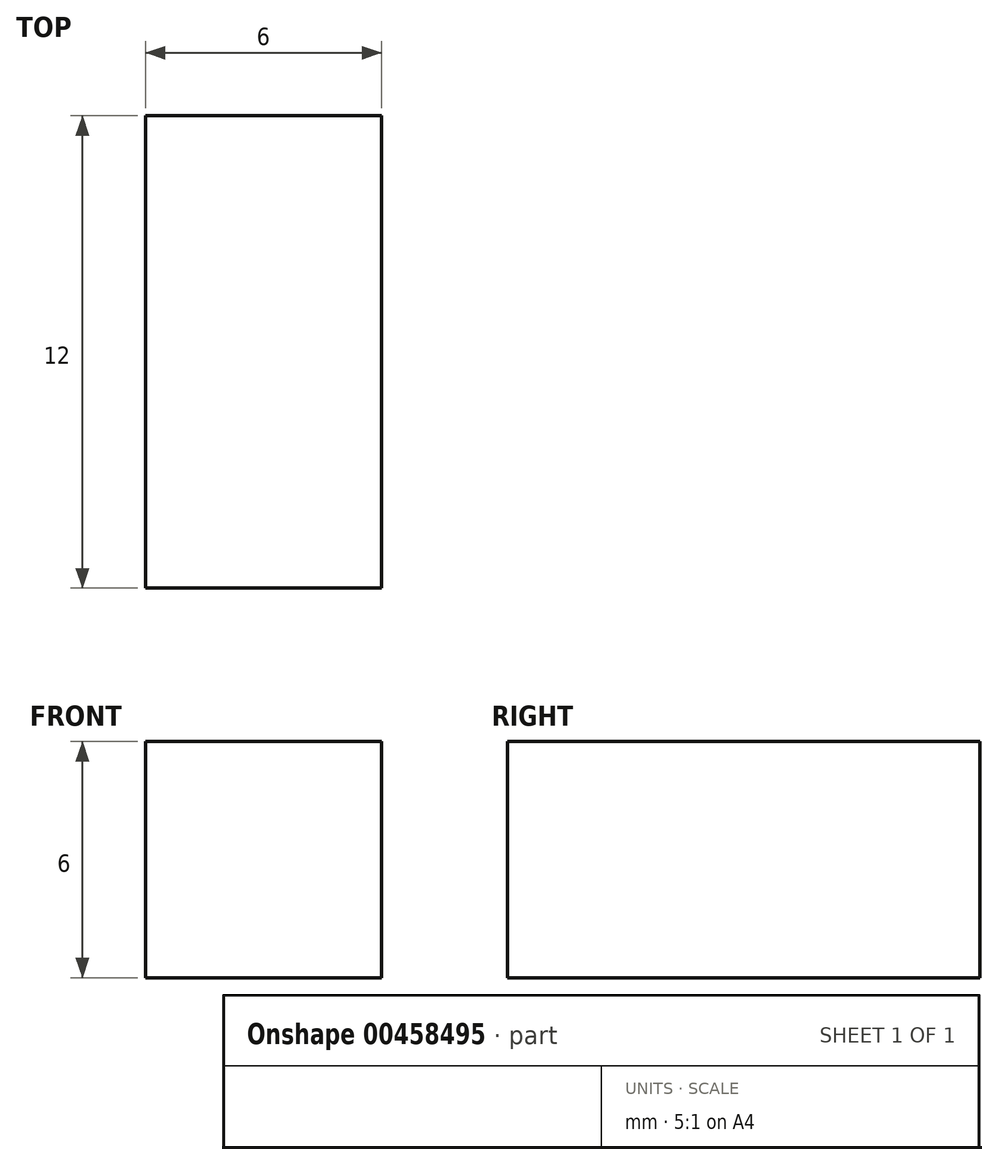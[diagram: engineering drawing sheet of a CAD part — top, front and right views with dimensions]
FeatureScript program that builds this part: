
annotation { "Feature Type Name" : "Feature", "Feature Type Description" : "" }
export const myFeature = defineFeature(function(context is Context, id is Id, definition is map)
    precondition{}
    {
        {
            var Q0;
            Q0=qCreatedBy(makeId("Front.planeOp"),FACE);
            var sketch = newSketch(context, id + "F0", { "sketchPlane" : qUnion([Q0])});
            skLineSegment(sketch, "E0", {"start": v(0, 0) * mm, "end": v(3, 0) * mm});
            skLineSegment(sketch, "E1", {"start": v(3, 0) * mm, "end": v(3, 6) * mm});
            skLineSegment(sketch, "E2", {"start": v(-3, 6) * mm, "end": v(3, 6) * mm});
            skLineSegment(sketch, "E3", {"start": v(-3, 6) * mm, "end": v(-3, 0) * mm});
            skLineSegment(sketch, "E4", {"start": v(3, 6) * mm, "end": v(-3, 6) * mm});
            skLineSegment(sketch, "E5", {"start": v(-3, 0) * mm, "end": v(0, 0) * mm});
            skSolve(sketch);
        }
        {
            var Q0;
            Q0=makeQuery(id+"F0.imprint","IMPRINT",FACE,{"disambiguationData":[TD([[makeQuery(id+"F0.imprint","IMPRINT",EDGE,{"derivedFrom":sQuery(id+"F0.wireOp",EDGE,"E0")}),1.0]])]});
            extrude(context, id + "F1", {"entities" : qUnion([Q0]), "depth" : 12 * mm});
        }
    });
